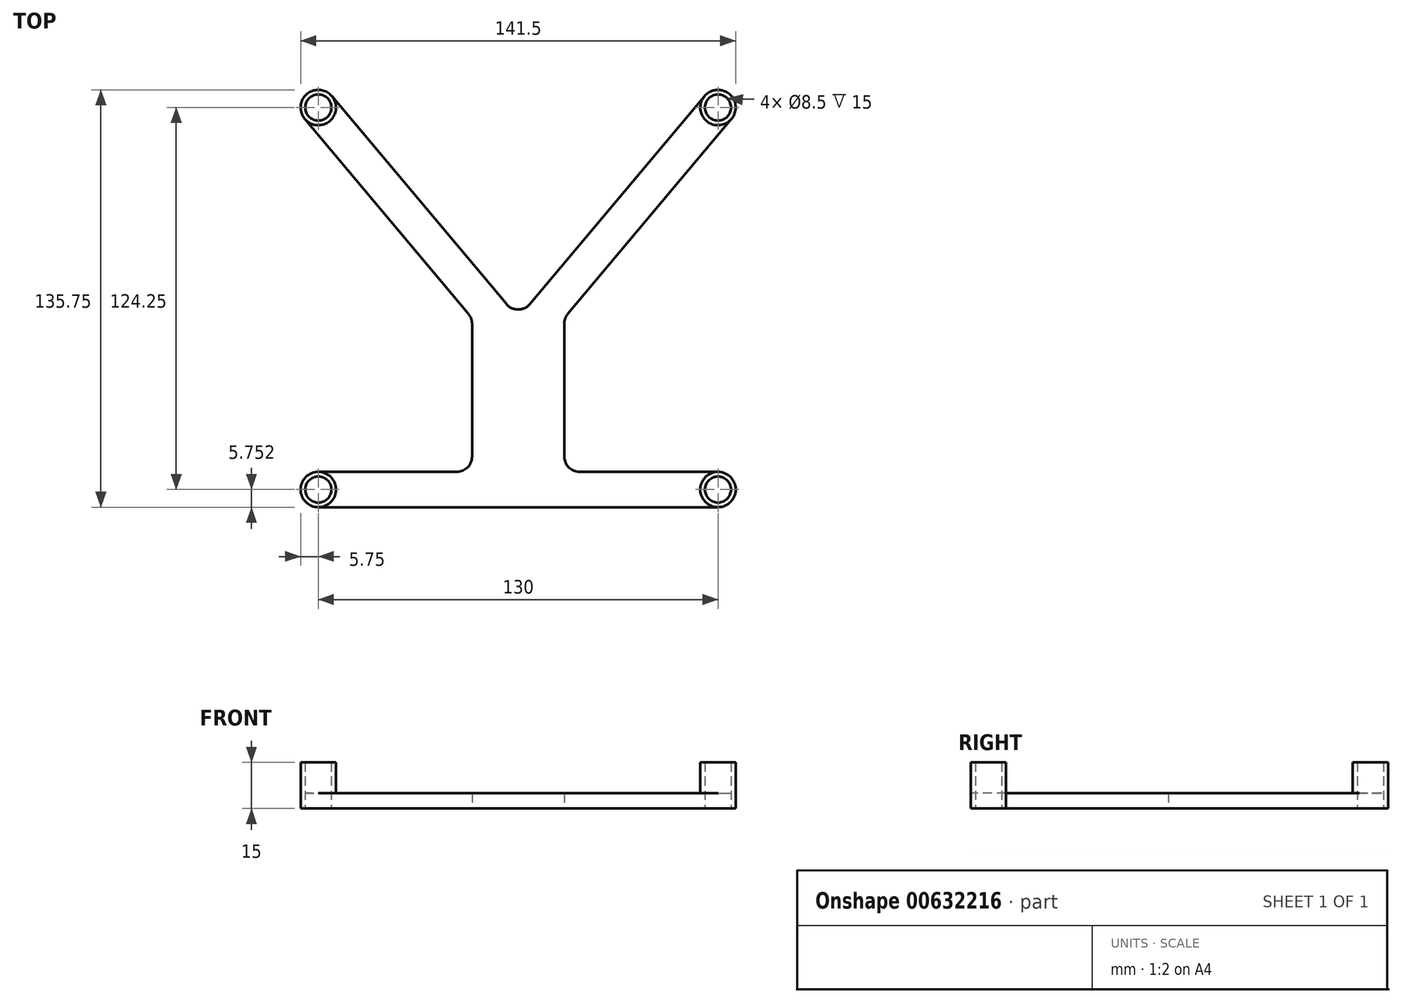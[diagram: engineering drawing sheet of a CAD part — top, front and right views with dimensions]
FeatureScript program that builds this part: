
annotation { "Feature Type Name" : "Feature", "Feature Type Description" : "" }
export const myFeature = defineFeature(function(context is Context, id is Id, definition is map)
    precondition{}
    {
        {
            var Q0;
            Q0=qCreatedBy(makeId("Top.planeOp"),FACE);
            var sketch = newSketch(context, id + "F0", { "sketchPlane" : qUnion([Q0])});
            skLineSegment(sketch, "E0", {"start": v(-15, -0.02) * mm, "end": v(-69.4, 64.78) * mm});
            skLineSegment(sketch, "E1", {"start": v(0, 0) * mm, "end": v(-60.6, 72.18) * mm});
            skLineSegment(sketch, "E2", {"start": v(-60.6, 72.18) * mm, "end": v(-69.4, 64.78) * mm});
            skLineSegment(sketch, "E3.top", {"start": v(60.6, 72.18) * mm, "end": v(69.4, 64.78) * mm});
            skLineSegment(sketch, "E3.left", {"start": v(0, 0) * mm, "end": v(60.6, 72.18) * mm});
            skLineSegment(sketch, "E3.right", {"start": v(15, -0.02) * mm, "end": v(69.4, 64.78) * mm});
            skLineSegment(sketch, "E4.top", {"start": v(15, -61.52) * mm, "end": v(-15, -61.52) * mm});
            skLineSegment(sketch, "E4.left", {"start": v(15, -0.02) * mm, "end": v(15, -50.02) * mm});
            skLineSegment(sketch, "E4.right", {"start": v(-15, -0.02) * mm, "end": v(-15, -50.02) * mm});
            skLineSegment(sketch, "E5.bottom", {"start": v(-15, -61.52) * mm, "end": v(-65, -61.52) * mm});
            skLineSegment(sketch, "E5.top", {"start": v(-15, -50.02) * mm, "end": v(-65, -50.02) * mm});
            skLineSegment(sketch, "E5.right", {"start": v(-65, -61.52) * mm, "end": v(-65, -50.02) * mm});
            skLineSegment(sketch, "E6.bottom", {"start": v(15, -61.52) * mm, "end": v(65, -61.52) * mm});
            skLineSegment(sketch, "E6.top", {"start": v(15, -50.02) * mm, "end": v(65, -50.02) * mm});
            skLineSegment(sketch, "E6.right", {"start": v(65, -61.52) * mm, "end": v(65, -50.02) * mm});
            skCircle(sketch, "E7", {"center": v(-65, -55.77) * mm, "radius": 4.25 * mm});
            skCircle(sketch, "E8", {"center": v(65, -55.77) * mm, "radius": 4.25 * mm});
            skCircle(sketch, "E9", {"center": v(-65, 68.48) * mm, "radius": 4.25 * mm});
            skCircle(sketch, "E10", {"center": v(65, 68.48) * mm, "radius": 4.25 * mm});
            skCircle(sketch, "E11", {"center": v(-65, -55.77) * mm, "radius": 5.75 * mm});
            skCircle(sketch, "E12", {"center": v(65, -55.77) * mm, "radius": 5.75 * mm});
            skCircle(sketch, "E13", {"center": v(-65, 68.48) * mm, "radius": 5.75 * mm});
            skCircle(sketch, "E14", {"center": v(65, 68.48) * mm, "radius": 5.75 * mm});
            skLineSegment(sketch, "E15", {"start": v(-65, 68.48) * mm, "end": v(-65, -42.27) * mm, "construction": true});
            skLineSegment(sketch, "E16", {"start": v(65, 68.48) * mm, "end": v(65, -23.68) * mm, "construction": true});
            skSolve(sketch);
        }
        {
            var Q0;
            {var subQ9=sQuery(id+"F0.wireOp",EDGE,"E0");Q0=makeQuery(id+"F0.imprint","IMPRINT",FACE,{"disambiguationData":[TD([[makeQuery(id+"F0.imprint","IMPRINT",EDGE,{"derivedFrom":subQ9}),-1.0]])]});}
            extrude(context, id + "F1", {"entities" : qUnion([Q0]), "depth" : 5 * mm, "offsetDistance" : 25 * mm});
        }
        {
            var Q0;
            {var subQ1=sQuery(id+"F0.wireOp",EDGE,"E5.right");var subQ3=sQuery(id+"F0.wireOp",EDGE,"E7");var subQ4=makeQuery(id+"F0.imprint","INTERSECT",VERTEX,{"disambiguationData":[OD(0.0)],"derivedFrom":[subQ1,subQ3]});Q0=makeQuery(id+"F0.imprint","IMPRINT",FACE,{"disambiguationData":[TD([[makeQuery(id+"F0.imprint","IMPRINT",EDGE,{"disambiguationData":[TD([[subQ4,-1.0]])],"derivedFrom":subQ3}),-1.0]])]});}
            var Q1;
            {var subQ1=sQuery(id+"F0.wireOp",EDGE,"E5.right");var subQ3=sQuery(id+"F0.wireOp",EDGE,"E7");var subQ4=makeQuery(id+"F0.imprint","INTERSECT",VERTEX,{"disambiguationData":[OD(0.0)],"derivedFrom":[subQ1,subQ3]});Q1=makeQuery(id+"F0.imprint","IMPRINT",FACE,{"disambiguationData":[TD([[makeQuery(id+"F0.imprint","IMPRINT",EDGE,{"disambiguationData":[TD([[subQ4,1.0]])],"derivedFrom":subQ3}),-1.0]])]});}
            var Q2;
            {var subQ1=sQuery(id+"F0.wireOp",EDGE,"E6.right");var subQ3=sQuery(id+"F0.wireOp",EDGE,"E8");var subQ4=makeQuery(id+"F0.imprint","INTERSECT",VERTEX,{"disambiguationData":[OD(0.0)],"derivedFrom":[subQ1,subQ3]});Q2=makeQuery(id+"F0.imprint","IMPRINT",FACE,{"disambiguationData":[TD([[makeQuery(id+"F0.imprint","IMPRINT",EDGE,{"disambiguationData":[TD([[subQ4,-1.0]])],"derivedFrom":subQ3}),-1.0]])]});}
            var Q3;
            {var subQ1=sQuery(id+"F0.wireOp",EDGE,"E6.right");var subQ3=sQuery(id+"F0.wireOp",EDGE,"E8");var subQ4=makeQuery(id+"F0.imprint","INTERSECT",VERTEX,{"disambiguationData":[OD(0.0)],"derivedFrom":[subQ1,subQ3]});Q3=makeQuery(id+"F0.imprint","IMPRINT",FACE,{"disambiguationData":[TD([[makeQuery(id+"F0.imprint","IMPRINT",EDGE,{"disambiguationData":[TD([[subQ4,1.0]])],"derivedFrom":subQ3}),-1.0]])]});}
            var Q4;
            {var subQ1=sQuery(id+"F0.wireOp",EDGE,"E3.top");var subQ3=sQuery(id+"F0.wireOp",EDGE,"E10");var subQ4=makeQuery(id+"F0.imprint","INTERSECT",VERTEX,{"disambiguationData":[OD(0.0)],"derivedFrom":[subQ1,subQ3]});Q4=makeQuery(id+"F0.imprint","IMPRINT",FACE,{"disambiguationData":[TD([[makeQuery(id+"F0.imprint","IMPRINT",EDGE,{"disambiguationData":[TD([[subQ4,1.0]])],"derivedFrom":subQ3}),-1.0]])]});}
            var Q5;
            {var subQ1=sQuery(id+"F0.wireOp",EDGE,"E3.top");var subQ3=sQuery(id+"F0.wireOp",EDGE,"E10");var subQ4=makeQuery(id+"F0.imprint","INTERSECT",VERTEX,{"disambiguationData":[OD(0.0)],"derivedFrom":[subQ1,subQ3]});Q5=makeQuery(id+"F0.imprint","IMPRINT",FACE,{"disambiguationData":[TD([[makeQuery(id+"F0.imprint","IMPRINT",EDGE,{"disambiguationData":[TD([[subQ4,-1.0]])],"derivedFrom":subQ3}),-1.0]])]});}
            var Q6;
            {var subQ1=sQuery(id+"F0.wireOp",EDGE,"E2");var subQ3=sQuery(id+"F0.wireOp",EDGE,"E9");var subQ4=makeQuery(id+"F0.imprint","INTERSECT",VERTEX,{"disambiguationData":[OD(0.0)],"derivedFrom":[subQ1,subQ3]});Q6=makeQuery(id+"F0.imprint","IMPRINT",FACE,{"disambiguationData":[TD([[makeQuery(id+"F0.imprint","IMPRINT",EDGE,{"disambiguationData":[TD([[subQ4,1.0]])],"derivedFrom":subQ3}),-1.0]])]});}
            var Q7;
            {var subQ1=sQuery(id+"F0.wireOp",EDGE,"E2");var subQ3=sQuery(id+"F0.wireOp",EDGE,"E9");var subQ4=makeQuery(id+"F0.imprint","INTERSECT",VERTEX,{"disambiguationData":[OD(0.0)],"derivedFrom":[subQ1,subQ3]});Q7=makeQuery(id+"F0.imprint","IMPRINT",FACE,{"disambiguationData":[TD([[makeQuery(id+"F0.imprint","IMPRINT",EDGE,{"disambiguationData":[TD([[subQ4,-1.0]])],"derivedFrom":subQ3}),-1.0]])]});}
            extrude(context, id + "F2", {"entities" : qUnion([Q0, Q1, Q2, Q3, Q4, Q5, Q6, Q7]), "operationType" : NewBodyOperationType.ADD, "depth" : 15 * mm, "offsetDistance" : 25 * mm});
        }
        {
            var Q0;
            Q0=makeQuery(id+"F1.opExtrude","SWEPT_EDGE",EDGE,{"disambiguationData":[OSD([sQuery(id+"F0.wireOp",EDGE,"E1"),sQuery(id+"F0.wireOp",EDGE,"E3.left")])]});
            var Q1;
            Q1=makeQuery(id+"F1.opExtrude","SWEPT_EDGE",EDGE,{"disambiguationData":[OSD([sQuery(id+"F0.wireOp",EDGE,"E0"),sQuery(id+"F0.wireOp",EDGE,"E4.right")])]});
            var Q2;
            Q2=makeQuery(id+"F1.opExtrude","SWEPT_EDGE",EDGE,{"disambiguationData":[OSD([sQuery(id+"F0.wireOp",EDGE,"E3.right"),sQuery(id+"F0.wireOp",EDGE,"E4.left")])]});
            var Q3;
            Q3=makeQuery(id+"F1.opExtrude","SWEPT_EDGE",EDGE,{"disambiguationData":[OSD([sQuery(id+"F0.wireOp",EDGE,"E4.left"),sQuery(id+"F0.wireOp",EDGE,"E6.top")])]});
            var Q4;
            Q4=makeQuery(id+"F1.opExtrude","SWEPT_EDGE",EDGE,{"disambiguationData":[OSD([sQuery(id+"F0.wireOp",EDGE,"E4.right"),sQuery(id+"F0.wireOp",EDGE,"E5.top")])]});
            fillet(context, id + "F3", {"entities" : qUnion([Q0, Q1, Q2, Q3, Q4]), "radius" : 5 * mm, "tangentPropagation" : true, "allowEdgeOverflow" : false});
        }
    });
